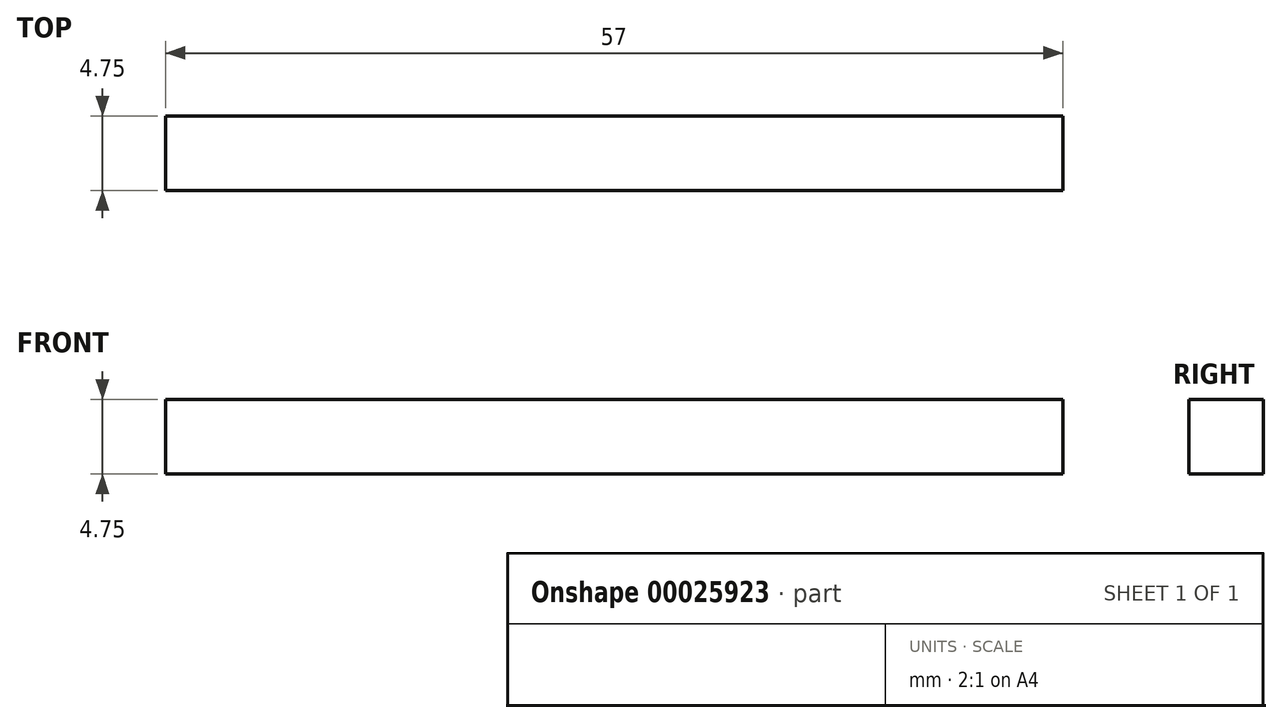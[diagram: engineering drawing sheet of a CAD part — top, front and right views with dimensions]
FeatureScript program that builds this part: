
annotation { "Feature Type Name" : "Feature", "Feature Type Description" : "" }
export const myFeature = defineFeature(function(context is Context, id is Id, definition is map)
    precondition{}
    {
        {
            var Q0;
            Q0=qCreatedBy(makeId("Front.planeOp"),FACE);
            var sketch = newSketch(context, id + "F0", { "sketchPlane" : qUnion([Q0])});
            skLineSegment(sketch, "E0.bottom", {"start": v(0, 0) * mm, "end": v(57, 0) * mm});
            skLineSegment(sketch, "E0.top", {"start": v(0, 4.75) * mm, "end": v(57, 4.75) * mm});
            skLineSegment(sketch, "E0.left", {"start": v(0, 0) * mm, "end": v(0, 4.75) * mm});
            skLineSegment(sketch, "E0.right", {"start": v(57, 0) * mm, "end": v(57, 4.75) * mm});
            skSolve(sketch);
        }
        {
            var Q0;
            Q0=makeQuery(id+"F0.imprint","IMPRINT",FACE,{"disambiguationData":[TD([[makeQuery(id+"F0.imprint","IMPRINT",EDGE,{"derivedFrom":sQuery(id+"F0.wireOp",EDGE,"E0.bottom")}),1.0]])]});
            extrude(context, id + "F1", {"entities" : qUnion([Q0]), "depth" : 4.75 * mm});
        }
    });
